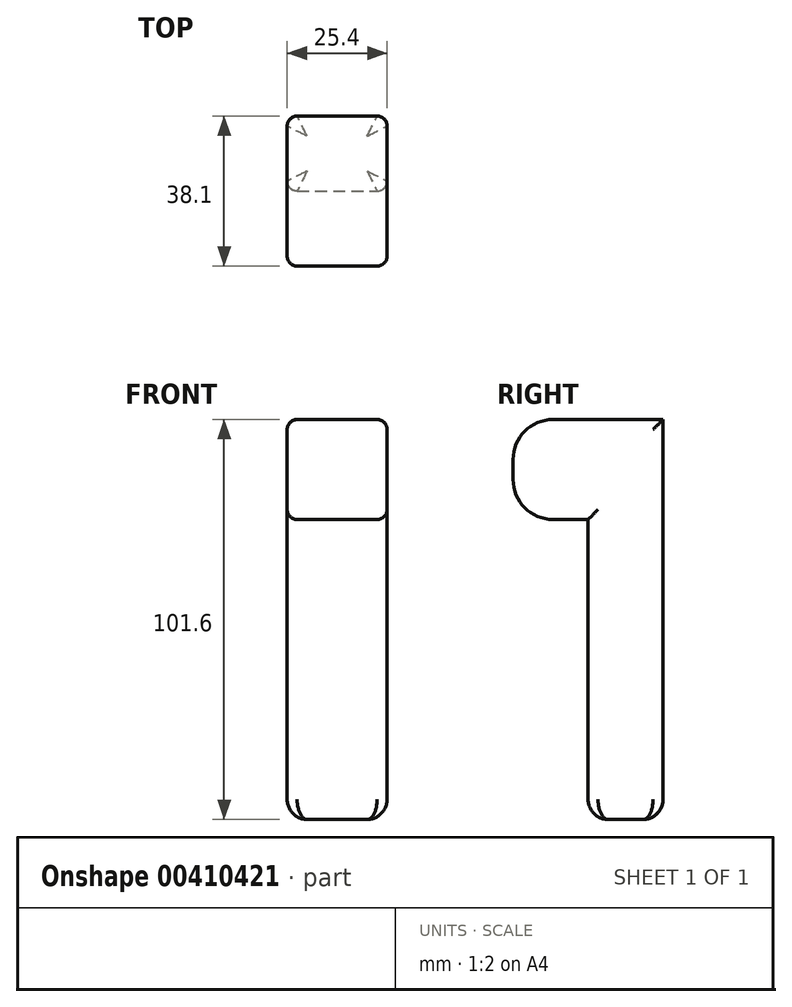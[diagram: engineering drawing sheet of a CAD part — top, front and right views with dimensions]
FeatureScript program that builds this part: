
annotation { "Feature Type Name" : "Feature", "Feature Type Description" : "" }
export const myFeature = defineFeature(function(context is Context, id is Id, definition is map)
    precondition{}
    {
        {
            var Q0;
            Q0=qCreatedBy(makeId("Top.planeOp"),FACE);
            var sketch = newSketch(context, id + "F0", { "sketchPlane" : qUnion([Q0])});
            skLineSegment(sketch, "E0.bottom", {"start": v(-12.7, 9.53) * mm, "end": v(12.7, 9.53) * mm});
            skLineSegment(sketch, "E0.top", {"start": v(-12.7, -9.53) * mm, "end": v(12.7, -9.53) * mm});
            skLineSegment(sketch, "E0.left", {"start": v(-12.7, 9.53) * mm, "end": v(-12.7, -9.53) * mm});
            skLineSegment(sketch, "E0.right", {"start": v(12.7, 9.53) * mm, "end": v(12.7, -9.53) * mm});
            skPoint(sketch, "E0.middle", {"position": v(0, 0) * mm});
            skSolve(sketch);
        }
        {
            var Q0;
            Q0 = qSketchRegion(id + "F0", true);
            extrude(context, id + "F1", {"entities" : qUnion([Q0]), "depth" : 101.6 * mm});
        }
        {
            var Q0;
            Q0=makeQuery(id+"F1.opExtrude","CAP_EDGE",EDGE,{"disambiguationData":[OSD([sQuery(id+"F0.wireOp",EDGE,"E0.top")])],"isStart":true});
            var Q1;
            Q1=makeQuery(id+"F1.opExtrude","CAP_EDGE",EDGE,{"disambiguationData":[OSD([sQuery(id+"F0.wireOp",EDGE,"E0.right")])],"isStart":true});
            var Q2;
            Q2=makeQuery(id+"F1.opExtrude","CAP_EDGE",EDGE,{"disambiguationData":[OSD([sQuery(id+"F0.wireOp",EDGE,"E0.bottom")])],"isStart":true});
            var Q3;
            Q3=makeQuery(id+"F1.opExtrude","CAP_EDGE",EDGE,{"disambiguationData":[OSD([sQuery(id+"F0.wireOp",EDGE,"E0.left")])],"isStart":true});
            fillet(context, id + "F2", {"entities" : qUnion([Q0, Q1, Q2, Q3]), "radius" : 5.08 * mm, "tangentPropagation" : true, "allowEdgeOverflow" : false});
        }
        {
            var Q0;
            Q0=makeQuery(id+"F1.opExtrude","SWEPT_FACE",FACE,{"disambiguationData":[OSD([sQuery(id+"F0.wireOp",EDGE,"E0.top")])]});
            var sketch = newSketch(context, id + "F3", { "sketchPlane" : qUnion([Q0])});
            skLineSegment(sketch, "E1.bottom", {"start": v(-12.7, 101.6) * mm, "end": v(12.7, 101.6) * mm});
            skLineSegment(sketch, "E1.top", {"start": v(-12.7, 76.2) * mm, "end": v(12.7, 76.2) * mm});
            skLineSegment(sketch, "E1.left", {"start": v(-12.7, 101.6) * mm, "end": v(-12.7, 76.2) * mm});
            skLineSegment(sketch, "E1.right", {"start": v(12.7, 101.6) * mm, "end": v(12.7, 76.2) * mm});
            skSolve(sketch);
        }
        {
            var Q0;
            Q0 = qSketchRegion(id + "F3", true);
            extrude(context, id + "F4", {"entities" : qUnion([Q0]), "operationType" : NewBodyOperationType.ADD, "depth" : 19.05 * mm});
        }
        {
            var Q0;
            Q0=makeQuery(id+"F4.opExtrude","CAP_EDGE",EDGE,{"disambiguationData":[OSD([sQuery(id+"F3.wireOp",EDGE,"E1.bottom")])],"isStart":false});
            var Q1;
            Q1=makeQuery(id+"F4.opExtrude","CAP_EDGE",EDGE,{"disambiguationData":[OSD([sQuery(id+"F3.wireOp",EDGE,"E1.top")])],"isStart":false});
            fillet(context, id + "F5", {"entities" : qUnion([Q0, Q1]), "radius" : 10.16 * mm, "tangentPropagation" : true, "allowEdgeOverflow" : false});
        }
        {
            var Q0;
            Q0=makeQuery(id+"F1.opExtrude","SWEPT_EDGE",EDGE,{"disambiguationData":[OSD([sQuery(id+"F0.wireOp",EDGE,"E0.bottom"),sQuery(id+"F0.wireOp",EDGE,"E0.right")])]});
            var Q1;
            Q1=makeQuery(id+"F1.opExtrude","SWEPT_EDGE",EDGE,{"disambiguationData":[OSD([sQuery(id+"F0.wireOp",EDGE,"E0.bottom"),sQuery(id+"F0.wireOp",EDGE,"E0.left")])]});
            var Q2;
            Q2=makeQuery(id+"F1.opExtrude","SWEPT_EDGE",EDGE,{"disambiguationData":[OSD([sQuery(id+"F0.wireOp",EDGE,"E0.top"),sQuery(id+"F0.wireOp",EDGE,"E0.left")])]});
            var Q3;
            Q3=makeQuery(id+"F1.opExtrude","SWEPT_EDGE",EDGE,{"disambiguationData":[OSD([sQuery(id+"F0.wireOp",EDGE,"E0.top"),sQuery(id+"F0.wireOp",EDGE,"E0.right")])]});
            var Q4;
            Q4=makeQuery(id+"F4.boolean.opBoolean","MERGE",EDGE,{"derivedFrom":[makeQuery(id+"F1.opExtrude","CAP_EDGE",EDGE,{"disambiguationData":[OSD([sQuery(id+"F0.wireOp",EDGE,"E0.right")])],"isStart":false}),makeQuery(id+"F4.opExtrude","SWEPT_EDGE",EDGE,{"disambiguationData":[OSD([sQuery(id+"F3.wireOp",EDGE,"E1.bottom"),sQuery(id+"F3.wireOp",EDGE,"E1.right")])]})]});
            var Q5;
            Q5=makeQuery(id+"F4.boolean.opBoolean","MERGE",EDGE,{"derivedFrom":[makeQuery(id+"F1.opExtrude","CAP_EDGE",EDGE,{"disambiguationData":[OSD([sQuery(id+"F0.wireOp",EDGE,"E0.left")])],"isStart":false}),makeQuery(id+"F4.opExtrude","SWEPT_EDGE",EDGE,{"disambiguationData":[OSD([sQuery(id+"F3.wireOp",EDGE,"E1.bottom"),sQuery(id+"F3.wireOp",EDGE,"E1.left")])]})]});
            fillet(context, id + "F6", {"entities" : qUnion([Q0, Q1, Q2, Q3, Q4, Q5]), "radius" : 2.54 * mm, "tangentPropagation" : true, "allowEdgeOverflow" : false});
        }
    });
